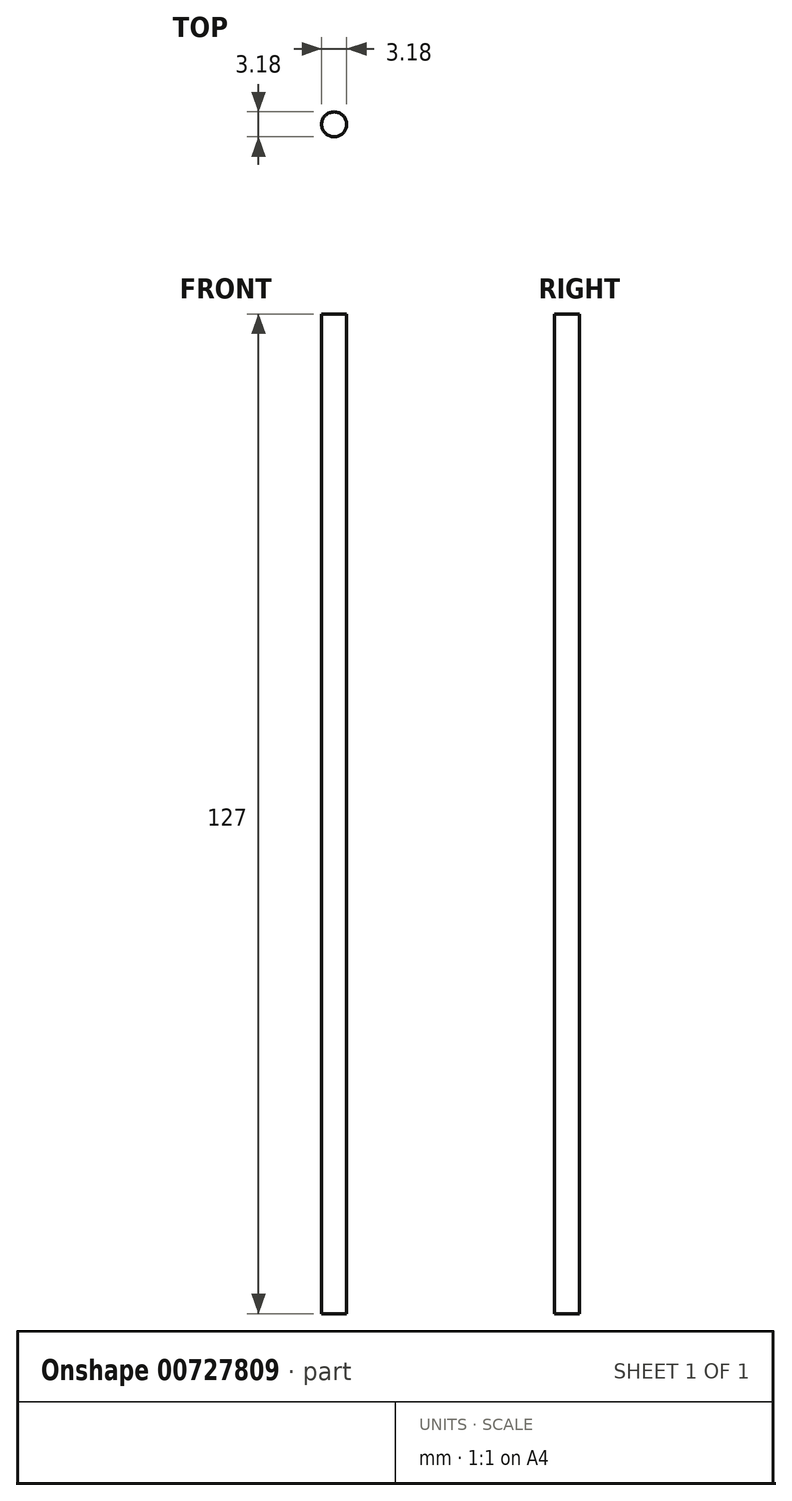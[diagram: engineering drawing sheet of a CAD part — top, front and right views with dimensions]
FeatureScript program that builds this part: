
annotation { "Feature Type Name" : "Feature", "Feature Type Description" : "" }
export const myFeature = defineFeature(function(context is Context, id is Id, definition is map)
    precondition{}
    {
        {
            var Q0;
            Q0=qCreatedBy(makeId("Top.planeOp"),FACE);
            var sketch = newSketch(context, id + "F0", { "sketchPlane" : qUnion([Q0])});
            skCircle(sketch, "E0", {"center": v(0, 0) * mm, "radius": 1.59 * mm});
            skSolve(sketch);
        }
        {
            var Q0;
            Q0=makeQuery(id+"F0.imprint","IMPRINT",FACE,{"disambiguationData":[TD([[makeQuery(id+"F0.imprint","IMPRINT",EDGE,{"derivedFrom":sQuery(id+"F0.wireOp",EDGE,"E0")}),1.0]])]});
            extrude(context, id + "F1", {"entities" : qUnion([Q0]), "depth" : 127 * mm, "offsetDistance" : 25.4 * mm});
        }
    });
